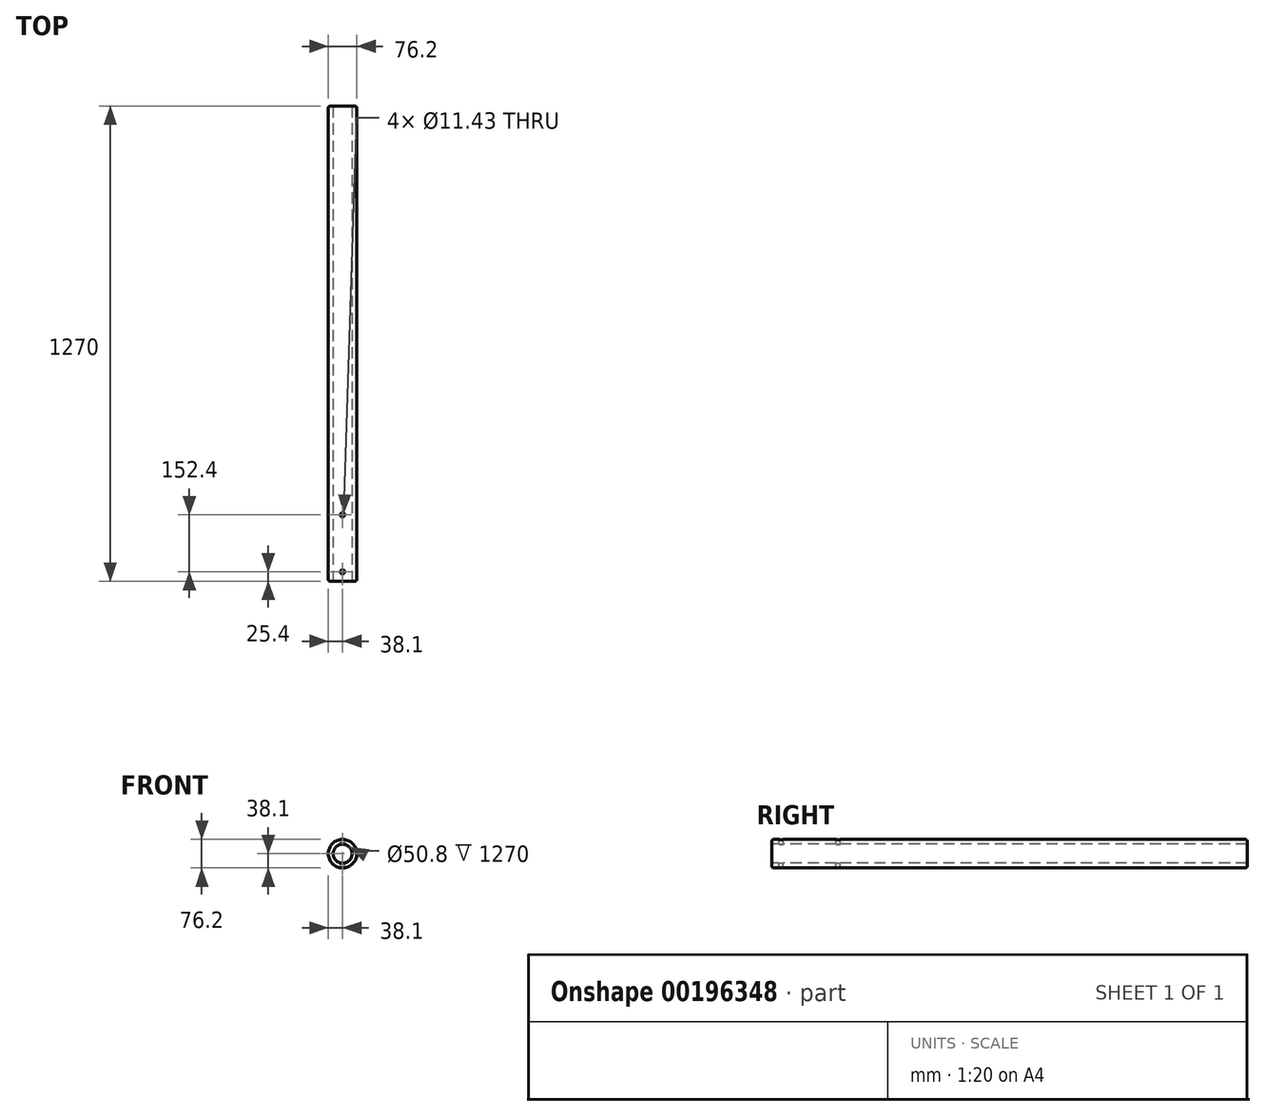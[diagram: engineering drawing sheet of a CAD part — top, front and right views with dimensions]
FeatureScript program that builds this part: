
annotation { "Feature Type Name" : "Feature", "Feature Type Description" : "" }
export const myFeature = defineFeature(function(context is Context, id is Id, definition is map)
    precondition{}
    {
        {
            var Q0;
            Q0=qCreatedBy(makeId("Front.planeOp"),FACE);
            var sketch = newSketch(context, id + "F0", { "sketchPlane" : qUnion([Q0])});
            skCircle(sketch, "E0", {"center": v(0, 0) * mm, "radius": 38.1 * mm});
            skSolve(sketch);
        }
        {
            var Q0;
            Q0 = qSketchRegion(id + "F0", true);
            extrude(context, id + "F1", {"entities" : qUnion([Q0]), "oppositeDirection" : true, "depth" : 1270 * mm});
        }
        {
            var Q0;
            Q0=makeQuery(id+"F1.opExtrude","CAP_FACE",FACE,{"disambiguationData":[OSD([sQuery(id+"F0.wireOp",EDGE,"E0")])],"isStart":true});
            var sketch = newSketch(context, id + "F2", { "sketchPlane" : qUnion([Q0])});
            skCircle(sketch, "E1", {"center": v(0, 0) * mm, "radius": 25.4 * mm});
            skSolve(sketch);
        }
        {
            var Q0;
            Q0 = qSketchRegion(id + "F2", true);
            extrude(context, id + "F3", {"entities" : qUnion([Q0]), "operationType" : NewBodyOperationType.REMOVE, "endBound" : BoundingType.THROUGH_ALL, "oppositeDirection" : true, "depth" : 25.4 * mm});
        }
        {
            var Q0;
            Q0=makeQuery(id+"F1.opExtrude","CAP_EDGE",EDGE,{"disambiguationData":[OSD([sQuery(id+"F0.wireOp",EDGE,"E0")])],"isStart":true});
            var Q1;
            Q1=makeQuery(id+"F1.opExtrude","CAP_EDGE",EDGE,{"disambiguationData":[OSD([sQuery(id+"F0.wireOp",EDGE,"E0")])],"isStart":false});
            fillet(context, id + "F4", {"entities" : qUnion([Q0, Q1]), "radius" : 5.08 * mm, "tangentPropagation" : true, "allowEdgeOverflow" : false});
        }
        {
            var Q0;
            Q0=qCreatedBy(makeId("Top.planeOp"),FACE);
            var sketch = newSketch(context, id + "F5", { "sketchPlane" : qUnion([Q0])});
            skLineSegment(sketch, "E2", {"start": v(0, 0) * mm, "end": v(0, 19.69) * mm});
            skCircle(sketch, "E3", {"center": v(0, 177.8) * mm, "radius": 5.72 * mm});
            skCircle(sketch, "E4", {"center": v(0, 25.4) * mm, "radius": 5.72 * mm});
            skLineSegment(sketch, "E5.trimOffspring", {"start": v(0, 31.12) * mm, "end": v(0, 177.8) * mm});
            skSolve(sketch);
        }
        {
            var Q0;
            Q0 = qSketchRegion(id + "F5", true);
            extrude(context, id + "F6", {"entities" : qUnion([Q0]), "operationType" : NewBodyOperationType.REMOVE, "endBound" : BoundingType.SYMMETRIC, "oppositeDirection" : true, "depth" : 76.2 * mm});
        }
    });
